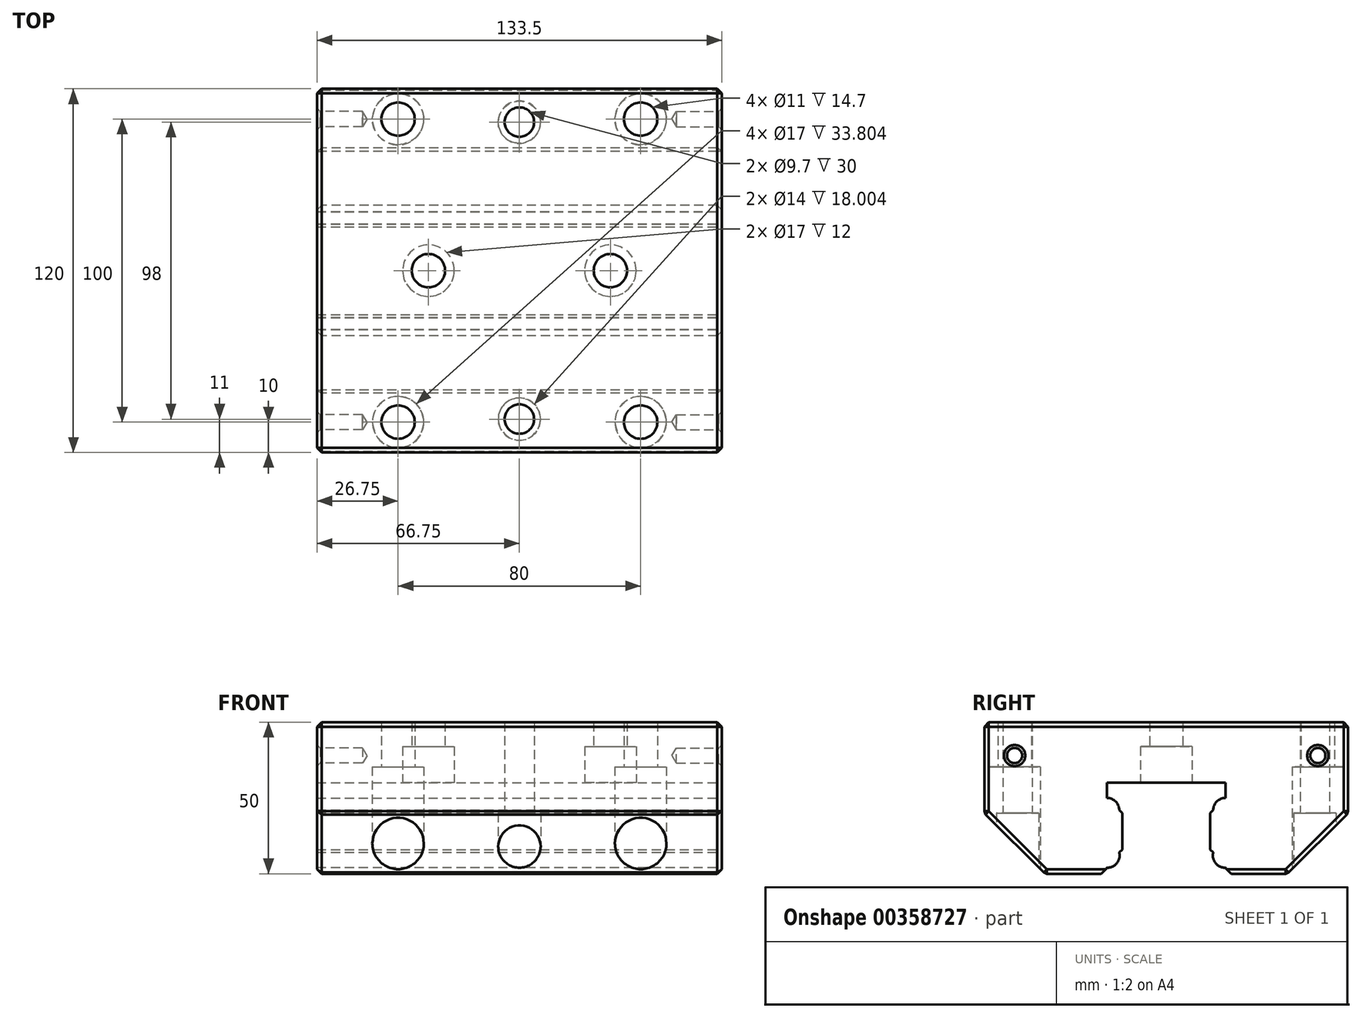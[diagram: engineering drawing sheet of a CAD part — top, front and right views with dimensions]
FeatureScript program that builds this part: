
annotation { "Feature Type Name" : "Feature", "Feature Type Description" : "" }
export const myFeature = defineFeature(function(context is Context, id is Id, definition is map)
    precondition{}
    {
        {
            var Q0;
            Q0=qCreatedBy(makeId("Front.planeOp"),FACE);
            var sketch = newSketch(context, id + "F0", { "sketchPlane" : qUnion([Q0])});
            skLineSegment(sketch, "E0.bottom", {"start": v(66.75, 25) * mm, "end": v(-66.75, 25) * mm});
            skLineSegment(sketch, "E0.top", {"start": v(66.75, -25) * mm, "end": v(-66.75, -25) * mm});
            skLineSegment(sketch, "E0.left", {"start": v(66.75, 25) * mm, "end": v(66.75, -25) * mm});
            skLineSegment(sketch, "E0.right", {"start": v(-66.75, 25) * mm, "end": v(-66.75, -25) * mm});
            skPoint(sketch, "E0.middle", {"position": v(0, 0) * mm});
            skSolve(sketch);
        }
        {
            var Q0;
            Q0=makeQuery(id+"F0.imprint","IMPRINT",FACE,{"disambiguationData":[TD([[makeQuery(id+"F0.imprint","IMPRINT",EDGE,{"derivedFrom":sQuery(id+"F0.wireOp",EDGE,"E0.bottom")}),1.0]])]});
            extrude(context, id + "F1", {"entities" : qUnion([Q0]), "depth" : 60 * mm});
        }
        {
            var Q0;
            Q0=makeQuery(id+"F1.opExtrude","SWEPT_FACE",FACE,{"disambiguationData":[OSD([sQuery(id+"F0.wireOp",EDGE,"E0.top")])]});
            var sketch = newSketch(context, id + "F2", { "sketchPlane" : qUnion([Q0])});
            skPoint(sketch, "E1", {"position": v(0, 49) * mm});
            skPoint(sketch, "E2", {"position": v(-40, 50) * mm});
            skPoint(sketch, "E3.MirrorP", {"position": v(40, 50) * mm});
            skPoint(sketch, "E4", {"position": v(-30, 0) * mm});
            skPoint(sketch, "E5.MirrorP", {"position": v(30, 0) * mm});
            skSolve(sketch);
        }
        {
            var Q0;
            Q0=sQuery(id+"F2.wireOp",VERTEX,"E2");
            var Q1;
            Q1=makeQuery(id+"F1.opExtrude","SWEPT_BODY",BODY,{"disambiguationData":[OSD([sQuery(id+"F0.wireOp",EDGE,"E0.bottom"),sQuery(id+"F0.wireOp",EDGE,"E0.top"),sQuery(id+"F0.wireOp",EDGE,"E0.left"),sQuery(id+"F0.wireOp",EDGE,"E0.right")])]});
            hole(context, id + "F3", {"style" : HoleStyle.C_BORE, "endStyle" : HoleEndStyle.THROUGH, "holeDiameter" : 11 * mm, "cBoreDiameter" : 17 * mm, "cBoreDepth" : (50 - 14.7) * mm, "isTappedThrough" : true, "tappedDepth" : 12 * mm, "tapClearance" : 3, "locations" : qUnion([Q0]), "scope" : qUnion([Q1])});
        }
        {
            var Q0;
            Q0=sQuery(id+"F2.wireOp",VERTEX,"E1");
            var Q1;
            Q1=makeQuery(id+"F1.opExtrude","SWEPT_BODY",BODY,{"disambiguationData":[OSD([sQuery(id+"F0.wireOp",EDGE,"E0.bottom"),sQuery(id+"F0.wireOp",EDGE,"E0.top"),sQuery(id+"F0.wireOp",EDGE,"E0.left"),sQuery(id+"F0.wireOp",EDGE,"E0.right")])]});
            hole(context, id + "F4", {"style" : HoleStyle.C_BORE, "endStyle" : HoleEndStyle.THROUGH, "holeDiameter" : 9.7 * mm, "cBoreDiameter" : 14 * mm, "cBoreDepth" : (50 - 30) * mm, "isTappedThrough" : true, "tappedDepth" : 12 * mm, "tapClearance" : 3, "startFromSketch" : true, "locations" : qUnion([Q0]), "scope" : qUnion([Q1])});
        }
        {
            var Q0;
            Q0=sQuery(id+"F2.wireOp",VERTEX,"E3.MirrorP");
            var Q1;
            Q1=makeQuery(id+"F1.opExtrude","SWEPT_BODY",BODY,{"disambiguationData":[OSD([sQuery(id+"F0.wireOp",EDGE,"E0.bottom"),sQuery(id+"F0.wireOp",EDGE,"E0.top"),sQuery(id+"F0.wireOp",EDGE,"E0.left"),sQuery(id+"F0.wireOp",EDGE,"E0.right")])]});
            hole(context, id + "F5", {"style" : HoleStyle.C_BORE, "endStyle" : HoleEndStyle.THROUGH, "holeDiameter" : 11 * mm, "cBoreDiameter" : 17 * mm, "cBoreDepth" : (50 - 14.7) * mm, "isTappedThrough" : true, "tappedDepth" : 12 * mm, "tapClearance" : 3, "locations" : qUnion([Q0]), "scope" : qUnion([Q1])});
        }
        {
            var Q0;
            Q0=makeQuery(id+"F1.opExtrude","CAP_EDGE",EDGE,{"disambiguationData":[OSD([sQuery(id+"F0.wireOp",EDGE,"E0.top")])],"isStart":false});
            chamfer(context, id + "F6", {"entities" : qUnion([Q0]), "width" : 20 * mm, "tangentPropagation" : true});
        }
        {
            var Q0;
            Q0=makeQuery(id+"F1.opExtrude","SWEPT_FACE",FACE,{"disambiguationData":[OSD([sQuery(id+"F0.wireOp",EDGE,"E0.left")])]});
            var sketch = newSketch(context, id + "F7", { "sketchPlane" : qUnion([Q0])});
            skPoint(sketch, "E6", {"position": v(-50, 14) * mm});
            skSolve(sketch);
        }
        {
            var Q0;
            Q0=sQuery(id+"F7.wireOp",VERTEX,"E6");
            var Q1;
            Q1=makeQuery(id+"F1.opExtrude","SWEPT_BODY",BODY,{"disambiguationData":[OSD([sQuery(id+"F0.wireOp",EDGE,"E0.bottom"),sQuery(id+"F0.wireOp",EDGE,"E0.top"),sQuery(id+"F0.wireOp",EDGE,"E0.left"),sQuery(id+"F0.wireOp",EDGE,"E0.right")])]});
            hole(context, id + "F8", {"style" : HoleStyle.C_SINK, "endStyle" : HoleEndStyle.BLIND, "holeDiameter" : 5 * mm, "cSinkDiameter" : 7 * mm, "cSinkAngle" : 90 * degree, "holeDepth" : 15 * mm, "isTappedThrough" : true, "tappedDepth" : 12 * mm, "tapClearance" : 3, "locations" : qUnion([Q0]), "scope" : qUnion([Q1])});
        }
        {
            var Q0;
            Q0=makeQuery(id+"F1.opExtrude","SWEPT_FACE",FACE,{"disambiguationData":[OSD([sQuery(id+"F0.wireOp",EDGE,"E0.right")])]});
            var sketch = newSketch(context, id + "F9", { "sketchPlane" : qUnion([Q0])});
            skPoint(sketch, "E7", {"position": v(50, 14) * mm});
            skSolve(sketch);
        }
        {
            var Q0;
            Q0=sQuery(id+"F9.wireOp",VERTEX,"E7");
            var Q1;
            Q1=makeQuery(id+"F1.opExtrude","SWEPT_BODY",BODY,{"disambiguationData":[OSD([sQuery(id+"F0.wireOp",EDGE,"E0.bottom"),sQuery(id+"F0.wireOp",EDGE,"E0.top"),sQuery(id+"F0.wireOp",EDGE,"E0.left"),sQuery(id+"F0.wireOp",EDGE,"E0.right")])]});
            hole(context, id + "F10", {"style" : HoleStyle.C_SINK, "endStyle" : HoleEndStyle.BLIND, "holeDiameter" : 5 * mm, "cSinkDiameter" : 7 * mm, "cSinkAngle" : 90 * degree, "holeDepth" : 15 * mm, "isTappedThrough" : true, "tappedDepth" : 12 * mm, "tapClearance" : 3, "locations" : qUnion([Q0]), "scope" : qUnion([Q1])});
        }
        {
            var Q0;
            Q0=makeQuery(id+"F1.opExtrude","SWEPT_EDGE",EDGE,{"disambiguationData":[OSD([sQuery(id+"F0.wireOp",EDGE,"E0.bottom"),sQuery(id+"F0.wireOp",EDGE,"E0.left")])]});
            var Q1;
            Q1=makeQuery(id+"F1.opExtrude","CAP_EDGE",EDGE,{"disambiguationData":[OSD([sQuery(id+"F0.wireOp",EDGE,"E0.bottom")])],"isStart":false});
            var Q2;
            Q2=makeQuery(id+"F1.opExtrude","CAP_EDGE",EDGE,{"disambiguationData":[OSD([sQuery(id+"F0.wireOp",EDGE,"E0.left")])],"isStart":false});
            var Q3;
            {var subQ0=sQuery(id+"F0.wireOp",EDGE,"E0.top");Q3=makeQuery(id+"F6.opChamfer","BLEND_EDGE",EDGE,{"blendedFrom":[makeQuery(id+"F1.opExtrude","CAP_EDGE",EDGE,{"disambiguationData":[OSD([subQ0])],"isStart":false}),makeQuery(id+"F1.opExtrude","CAP_FACE",FACE,{"disambiguationData":[OSD([sQuery(id+"F0.wireOp",EDGE,"E0.bottom"),subQ0,sQuery(id+"F0.wireOp",EDGE,"E0.left"),sQuery(id+"F0.wireOp",EDGE,"E0.right")])],"isStart":false})],"blendedInto":[makeQuery(id+"F1.opExtrude","CAP_FACE",FACE,{"disambiguationData":[OSD([sQuery(id+"F0.wireOp",EDGE,"E0.bottom"),subQ0,sQuery(id+"F0.wireOp",EDGE,"E0.left"),sQuery(id+"F0.wireOp",EDGE,"E0.right")])],"isStart":false})]});}
            var Q4;
            Q4=makeQuery(id+"F1.opExtrude","SWEPT_EDGE",EDGE,{"disambiguationData":[OSD([sQuery(id+"F0.wireOp",EDGE,"E0.top"),sQuery(id+"F0.wireOp",EDGE,"E0.right")])]});
            var Q5;
            Q5=makeQuery(id+"F6.opChamfer","BLEND_EDGE",EDGE,{"blendedFrom":[makeQuery(id+"F1.opExtrude","CAP_EDGE",EDGE,{"disambiguationData":[OSD([sQuery(id+"F0.wireOp",EDGE,"E0.top")])],"isStart":false}),makeQuery(id+"F1.opExtrude","SWEPT_FACE",FACE,{"disambiguationData":[OSD([sQuery(id+"F0.wireOp",EDGE,"E0.right")])]})],"blendedInto":[makeQuery(id+"F1.opExtrude","SWEPT_FACE",FACE,{"disambiguationData":[OSD([sQuery(id+"F0.wireOp",EDGE,"E0.right")])]})]});
            var Q6;
            Q6=makeQuery(id+"F1.opExtrude","CAP_EDGE",EDGE,{"disambiguationData":[OSD([sQuery(id+"F0.wireOp",EDGE,"E0.right")])],"isStart":false});
            var Q7;
            Q7=makeQuery(id+"F1.opExtrude","SWEPT_EDGE",EDGE,{"disambiguationData":[OSD([sQuery(id+"F0.wireOp",EDGE,"E0.bottom"),sQuery(id+"F0.wireOp",EDGE,"E0.right")])]});
            var Q8;
            Q8=makeQuery(id+"F6.opChamfer","BLEND_EDGE",EDGE,{"blendedFrom":[makeQuery(id+"F1.opExtrude","CAP_EDGE",EDGE,{"disambiguationData":[OSD([sQuery(id+"F0.wireOp",EDGE,"E0.top")])],"isStart":false}),makeQuery(id+"F1.opExtrude","SWEPT_FACE",FACE,{"disambiguationData":[OSD([sQuery(id+"F0.wireOp",EDGE,"E0.left")])]})],"blendedInto":[makeQuery(id+"F1.opExtrude","SWEPT_FACE",FACE,{"disambiguationData":[OSD([sQuery(id+"F0.wireOp",EDGE,"E0.left")])]})]});
            var Q9;
            {var subQ0=sQuery(id+"F0.wireOp",EDGE,"E0.top");Q9=makeQuery(id+"F6.opChamfer","BLEND_EDGE",EDGE,{"blendedFrom":[makeQuery(id+"F1.opExtrude","CAP_EDGE",EDGE,{"disambiguationData":[OSD([subQ0])],"isStart":false}),makeQuery(id+"F1.opExtrude","SWEPT_FACE",FACE,{"disambiguationData":[OSD([subQ0])]})],"blendedInto":[makeQuery(id+"F1.opExtrude","SWEPT_FACE",FACE,{"disambiguationData":[OSD([subQ0])]})]});}
            var Q10;
            Q10=makeQuery(id+"F1.opExtrude","SWEPT_EDGE",EDGE,{"disambiguationData":[OSD([sQuery(id+"F0.wireOp",EDGE,"E0.top"),sQuery(id+"F0.wireOp",EDGE,"E0.left")])]});
            chamfer(context, id + "F11", {"entities" : qUnion([Q0, Q1, Q2, Q3, Q4, Q5, Q6, Q7, Q8, Q9, Q10]), "width" : 1.5 * mm, "tangentPropagation" : true});
        }
        {
            var Q0;
            Q0=makeQuery(id+"F1.opExtrude","SWEPT_BODY",BODY,{"disambiguationData":[OSD([sQuery(id+"F0.wireOp",EDGE,"E0.bottom"),sQuery(id+"F0.wireOp",EDGE,"E0.top"),sQuery(id+"F0.wireOp",EDGE,"E0.left"),sQuery(id+"F0.wireOp",EDGE,"E0.right")])]});
            var Q1;
            Q1=qCreatedBy(makeId("Front.planeOp"),FACE);
            mirror(context, id + "F12", {"operationType" : NewBodyOperationType.ADD, "entities" : qUnion([Q0]), "mirrorPlane" : qUnion([Q1])});
        }
        {
            var Q0;
            Q0=sQuery(id+"F2.wireOp",VERTEX,"E4");
            var Q1;
            Q1=makeQuery(id+"F1.opExtrude","SWEPT_BODY",BODY,{"disambiguationData":[OSD([sQuery(id+"F0.wireOp",EDGE,"E0.bottom"),sQuery(id+"F0.wireOp",EDGE,"E0.top"),sQuery(id+"F0.wireOp",EDGE,"E0.left"),sQuery(id+"F0.wireOp",EDGE,"E0.right")])]});
            hole(context, id + "F13", {"style" : HoleStyle.C_BORE, "endStyle" : HoleEndStyle.THROUGH, "holeDiameter" : 11 * mm, "cBoreDiameter" : 17 * mm, "cBoreDepth" : (50 - 8) * mm, "isTappedThrough" : true, "tappedDepth" : 12 * mm, "tapClearance" : 3, "locations" : qUnion([Q0]), "scope" : qUnion([Q1])});
        }
        {
            var Q0;
            Q0=sQuery(id+"F2.wireOp",VERTEX,"E5.MirrorP");
            var Q1;
            Q1=makeQuery(id+"F1.opExtrude","SWEPT_BODY",BODY,{"disambiguationData":[OSD([sQuery(id+"F0.wireOp",EDGE,"E0.bottom"),sQuery(id+"F0.wireOp",EDGE,"E0.top"),sQuery(id+"F0.wireOp",EDGE,"E0.left"),sQuery(id+"F0.wireOp",EDGE,"E0.right")])]});
            hole(context, id + "F14", {"style" : HoleStyle.C_BORE, "endStyle" : HoleEndStyle.THROUGH, "holeDiameter" : 11 * mm, "cBoreDiameter" : 17 * mm, "cBoreDepth" : (50 - 8) * mm, "isTappedThrough" : true, "tappedDepth" : 12 * mm, "tapClearance" : 3, "locations" : qUnion([Q0]), "scope" : qUnion([Q1])});
        }
        {
            var Q0;
            {var subQ0=makeQuery(id+"F1.opExtrude","SWEPT_FACE",FACE,{"disambiguationData":[OSD([sQuery(id+"F0.wireOp",EDGE,"E0.left")])]});Q0=makeQuery(id+"F12.boolean.opBoolean","MERGE",FACE,{"derivedFrom":[subQ0,makeQuery(id+"F12.opPattern","COPY",FACE,{"derivedFrom":subQ0,"instanceName":"1"})]});}
            var sketch = newSketch(context, id + "F15", { "sketchPlane" : qUnion([Q0])});
            skLineSegment(sketch, "E8", {"start": v(0, -35) * mm, "end": v(-22.5, -35) * mm});
            skLineSegment(sketch, "E9", {"start": v(-22.5, -35) * mm, "end": v(-22.5, -26) * mm});
            skLineSegment(sketch, "E10", {"start": v(-19.37, -22.87) * mm, "end": v(-22.5, -26) * mm});
            skLineSegment(sketch, "E11", {"start": v(-19.37, -23) * mm, "end": v(-19.37, -22.87) * mm});
            skArc(sketch, "E12", {"start": v(-19.37, -23) * mm, "mid": v(-16.21, -21.45) * mm, "end": v(-15.5, -18) * mm});
            skLineSegment(sketch, "E13", {"start": v(-15.5, -18) * mm, "end": v(-14.5, -17) * mm});
            skLineSegment(sketch, "E14", {"start": v(-14.5, -17) * mm, "end": v(-14.5, -5) * mm});
            skLineSegment(sketch, "E15", {"start": v(-14.5, -5) * mm, "end": v(-15.5, -4) * mm});
            skArc(sketch, "E16", {"start": v(-15.5, -4) * mm, "mid": v(-16.67, -1.17) * mm, "end": v(-19.5, 0) * mm});
            skLineSegment(sketch, "E17", {"start": v(-19.5, 0) * mm, "end": v(-19.5, 5) * mm});
            skLineSegment(sketch, "E18", {"start": v(-19.5, 5) * mm, "end": v(0, 5) * mm});
            skLineSegment(sketch, "E19.MirrorCS", {"start": v(19.5, 5) * mm, "end": v(0, 5) * mm});
            skLineSegment(sketch, "E20.MirrorCS", {"start": v(19.5, 0) * mm, "end": v(19.5, 5) * mm});
            skArc(sketch, "E21.MirrorCS", {"start": v(15.5, -4) * mm, "mid": v(16.67, -1.17) * mm, "end": v(19.5, 0) * mm});
            skLineSegment(sketch, "E22.MirrorCS", {"start": v(14.5, -5) * mm, "end": v(15.5, -4) * mm});
            skLineSegment(sketch, "E23.MirrorCS", {"start": v(14.5, -17) * mm, "end": v(14.5, -5) * mm});
            skLineSegment(sketch, "E24.MirrorCS", {"start": v(15.5, -18) * mm, "end": v(14.5, -17) * mm});
            skArc(sketch, "E25.MirrorCS", {"start": v(19.37, -23) * mm, "mid": v(16.21, -21.45) * mm, "end": v(15.5, -18) * mm});
            skLineSegment(sketch, "E26.MirrorCS", {"start": v(19.37, -22.87) * mm, "end": v(22.5, -26) * mm});
            skLineSegment(sketch, "E27.MirrorCS", {"start": v(22.5, -35) * mm, "end": v(22.5, -26) * mm});
            skLineSegment(sketch, "E28.MirrorCS", {"start": v(0, -35) * mm, "end": v(22.5, -35) * mm});
            skLineSegment(sketch, "E29.MirrorCS", {"start": v(19.37, -23) * mm, "end": v(19.37, -22.87) * mm});
            skSolve(sketch);
        }
        {
            var Q0;
            Q0 = qSketchRegion(id + "F15", true);
            var Q1;
            {var subQ0=makeQuery(id+"F1.opExtrude","SWEPT_FACE",FACE,{"disambiguationData":[OSD([sQuery(id+"F0.wireOp",EDGE,"E0.right")])]});Q1=makeQuery(id+"F12.boolean.opBoolean","MERGE",FACE,{"derivedFrom":[subQ0,makeQuery(id+"F12.opPattern","COPY",FACE,{"derivedFrom":subQ0,"instanceName":"1"})]});}
            extrude(context, id + "F16", {"entities" : qUnion([Q0]), "operationType" : NewBodyOperationType.REMOVE, "endBound" : BoundingType.UP_TO_SURFACE, "oppositeDirection" : true, "endBoundEntityFace" : qUnion([Q1]), "depth" : 25 * mm});
        }
    });
